# Revit family: ROTHOB_Rothoblaas_Screw_HBSPlate-HBSPL
name_source: partatom
category: Structural Connections
units: mm (PartAtom-declared; Revit-internal decimal feet)

## family parameters
Cut with Voids When Loaded = No
Enable cutting in views = Yes
Host = Face
Material for Model Behavior = Steel
OmniClass Number = 23.20.40.11.14.24
OmniClass Title = Screws
Shared = No

## types (18) — shared parameters
AssetType = Fixed
BIMObjectName = ROTHOB_Rothoblaas_Screw_HBSPlate-HBSPL
CECode = ETA-11/0030
CETitle = Rotho Blaas Self-tapping screws and threaded rods
Category = Pr_20_29_76_75: Self-tapping screws
CodePerformance = CE - Construction products
Color = Silver
Default Elevation = 1219.2 mm
Description = Pan head screws for plates
DurationUnit = Years
Esporta tipo in formato IFC con nome = IfcMechanicalFastenerType
ExpectedLife = 50
Features = Self-tapping screws for steel-timber connections
Finish = Zinc plated
HeadType = Reinforced pan head
ICC-ESCode = ESR-4645 | ELC-4645
ICC-ESTitle = Rotho blaas self-tapping wood screws | Rotho Blaas Self-tapping Wood Screws
IfcExportAs = IfcMechanicalFastenerType
IfcExportType = USERDEFINED
ManufacturerName = ROTHO BLAAS SRL
ManufacturerURL = www.rothoblaas.com
Material = Electrogalvanized carbon steel
ModelDisclaimer = The latest version of the data sheets can be found on our website
Name = Screw
ObjectMaterial = ROTHOB_Rothoblaas_CarbonSteel_Electrogalvanized
OmniClassCode = 23.20.40.11.14.24
OmniClassTitle = Screws
OmniClassVersion = 2012-05-16
ProductInformation = www.rothoblaas.com/products/fastening/screws/screws-carpentry/hbs-plate
Revision = 000
Shape = Cylindrical
Tipo IFC predefinito = USERDEFINED
UniClass2015Code = Pr_20_29_76_75
UniClass2015Title = Self-tapping screws
UniClass2015Version = Products v1.38
Version = 003

## per-type parameters (varying)
| type | BitType | GTIN | H1 | H2 | HeadDiameter_dk | HeadThickness_t1 | InsertionLength_L | MinWeight | ModelNumber | ModelNumberCode | NominalDiameter | NominalDiameter_d1 | NominalLength | ShankDiameter_ds | ShankLength | Size | ThreadDiameter_d2 | ThreadLength_b | ThreadRadius | TipLength | UnderheadDiameter | UnderheadLength | WasherThickness_tk |
| HBSPL860_8x60mm | 40 | 8059386079140 | 5 mm  [stored 0.0164042 ft] | 2.0141 mm  [stored 0.00660794 ft] | 13.5 mm  [stored 0.0442913 ft] | 13.5 mm  [stored 0.0442913 ft] | 60 mm | 0.014 kg | HBSPL860 | 860 | 8 mm  [stored 0.0262467 ft] | 8 mm  [stored 0.0262467 ft] | 60 mm | 6.3 mm  [stored 0.0206693 ft] | 1 mm  [stored 0.00328084 ft] | 8x60 mm | 5.9 mm  [stored 0.019357 ft] | 52 mm | 2.95 mm  [stored 0.00967848 ft] | 11.8318 mm  [stored 0.0388182 ft] | 10 mm  [stored 0.0328084 ft] | 4 mm  [stored 0.0131234 ft] | 4.5 mm  [stored 0.0147638 ft] |
| HBSPL880_8x80mm | 40 | 8059386079188 | 5 mm  [stored 0.0164042 ft] | 2.0141 mm  [stored 0.00660794 ft] | 13.5 mm  [stored 0.0442913 ft] | 13.5 mm  [stored 0.0442913 ft] | 80 mm | 0.027 kg | HBSPL880 | 880 | 8 mm  [stored 0.0262467 ft] | 8 mm  [stored 0.0262467 ft] | 80 mm | 6.3 mm  [stored 0.0206693 ft] | 14.9929 mm  [stored 0.0491893 ft] | 8x80 mm | 5.9 mm  [stored 0.019357 ft] | 55 mm  [stored 0.180446 ft] | 2.95 mm  [stored 0.00967848 ft] | 11.8318 mm  [stored 0.0388182 ft] | 10 mm  [stored 0.0328084 ft] | 4 mm  [stored 0.0131234 ft] | 4.5 mm  [stored 0.0147638 ft] |
| HBSPL8100_8x100mm | 40 | 8059386079164 | 5 mm  [stored 0.0164042 ft] | 2.0141 mm  [stored 0.00660794 ft] | 13.5 mm  [stored 0.0442913 ft] | 13.5 mm  [stored 0.0442913 ft] | 100 mm | 0.030 kg | HBSPL8100 | 8100 | 8 mm  [stored 0.0262467 ft] | 8 mm  [stored 0.0262467 ft] | 100 mm | 6.3 mm  [stored 0.0206693 ft] | 14.9929 mm  [stored 0.0491893 ft] | 8x100 mm | 5.9 mm  [stored 0.019357 ft] | 75 mm | 2.95 mm  [stored 0.00967848 ft] | 11.8318 mm  [stored 0.0388182 ft] | 10 mm  [stored 0.0328084 ft] | 4 mm  [stored 0.0131234 ft] | 4.5 mm  [stored 0.0147638 ft] |
| HBSPL8120_8x120mm | 40 | 8059386079058 | 5 mm  [stored 0.0164042 ft] | 2.0141 mm  [stored 0.00660794 ft] | 13.5 mm  [stored 0.0442913 ft] | 13.5 mm  [stored 0.0442913 ft] | 120 mm | 0.036 kg | HBSPL8120 | 8120 | 8 mm  [stored 0.0262467 ft] | 8 mm  [stored 0.0262467 ft] | 120 mm | 6.3 mm  [stored 0.0206693 ft] | 14.9929 mm  [stored 0.0491893 ft] | 8x120 mm | 5.9 mm  [stored 0.019357 ft] | 95 mm | 2.95 mm  [stored 0.00967848 ft] | 11.8318 mm  [stored 0.0388182 ft] | 10 mm  [stored 0.0328084 ft] | 4 mm  [stored 0.0131234 ft] | 4.5 mm  [stored 0.0147638 ft] |
| HBSPL8140_8x140mm | 40 | 8059386079195 | 5 mm  [stored 0.0164042 ft] | 2.0141 mm  [stored 0.00660794 ft] | 13.5 mm  [stored 0.0442913 ft] | 13.5 mm  [stored 0.0442913 ft] | 140 mm | 0.030 kg | HBSPL8140 | 8140 | 8 mm  [stored 0.0262467 ft] | 8 mm  [stored 0.0262467 ft] | 140 mm | 6.3 mm  [stored 0.0206693 ft] | 19.9929 mm  [stored 0.0655935 ft] | 8x140 mm | 5.9 mm  [stored 0.019357 ft] | 110 mm | 2.95 mm  [stored 0.00967848 ft] | 11.8318 mm  [stored 0.0388182 ft] | 10 mm  [stored 0.0328084 ft] | 4 mm  [stored 0.0131234 ft] | 4.5 mm  [stored 0.0147638 ft] |
| HBSPL8160_8x160mm | 40 | 8059386079089 | 5 mm  [stored 0.0164042 ft] | 2.0141 mm  [stored 0.00660794 ft] | 13.5 mm  [stored 0.0442913 ft] | 13.5 mm  [stored 0.0442913 ft] | 160 mm | 0.035 kg | HBSPL8160 | 8160 | 8 mm  [stored 0.0262467 ft] | 8 mm  [stored 0.0262467 ft] | 160 mm | 6.3 mm  [stored 0.0206693 ft] | 19.9929 mm  [stored 0.0655935 ft] | 8x160 mm | 5.9 mm  [stored 0.019357 ft] | 130 mm | 2.95 mm  [stored 0.00967848 ft] | 11.8318 mm  [stored 0.0388182 ft] | 10 mm  [stored 0.0328084 ft] | 4 mm  [stored 0.0131234 ft] | 4.5 mm  [stored 0.0147638 ft] |
| HBSPL1080_10x80mm | 40 | 8059386079201 | 6.5 mm | 1.5329 mm | 16.5 mm  [stored 0.0541339 ft] | 16.5 mm  [stored 0.0541339 ft] | 80 mm | 0.034 kg | HBSPL1080 | 1080 | 10 mm  [stored 0.0328084 ft] | 10 mm  [stored 0.0328084 ft] | 80 mm | 7.2 mm  [stored 0.023622 ft] | 7.7353 mm  [stored 0.0253783 ft] | 10x80 mm | 6.6 mm  [stored 0.0216535 ft] | 60 mm | 3.3 mm  [stored 0.0108268 ft] | 13.2356 mm  [stored 0.0434239 ft] | 12 mm  [stored 0.0393701 ft] | 5 mm  [stored 0.0164042 ft] | 5 mm  [stored 0.0164042 ft] |
| HBSPL10100_10x100mm | 40 | 8059386079072 | 6.5 mm | 1.5329 mm | 16.5 mm  [stored 0.0541339 ft] | 16.5 mm  [stored 0.0541339 ft] | 100 mm | 0.038 kg | HBSPL10100 | 10100 | 10 mm  [stored 0.0328084 ft] | 10 mm  [stored 0.0328084 ft] | 100 mm | 7.2 mm  [stored 0.023622 ft] | 12.7352 mm  [stored 0.0417822 ft] | 10x100 mm | 6.6 mm  [stored 0.0216535 ft] | 75 mm | 3.3 mm  [stored 0.0108268 ft] | 13.2356 mm  [stored 0.0434239 ft] | 12 mm  [stored 0.0393701 ft] | 5 mm  [stored 0.0164042 ft] | 5 mm  [stored 0.0164042 ft] |
| HBSPL10120_10x120mm | 40 | 8059386079133 | 6.5 mm | 1.5329 mm | 16.5 mm  [stored 0.0541339 ft] | 16.5 mm  [stored 0.0541339 ft] | 120 mm | 0.046 kg | HBSPL10120 | 10120 | 10 mm  [stored 0.0328084 ft] | 10 mm  [stored 0.0328084 ft] | 120 mm | 7.2 mm  [stored 0.023622 ft] | 12.7352 mm  [stored 0.0417822 ft] | 10x120 mm | 6.6 mm  [stored 0.0216535 ft] | 95 mm | 3.3 mm  [stored 0.0108268 ft] | 13.2356 mm  [stored 0.0434239 ft] | 12 mm  [stored 0.0393701 ft] | 5 mm  [stored 0.0164042 ft] | 5 mm  [stored 0.0164042 ft] |
| HBSPL10140_10x140mm | 40 | 8059386079065 | 6.5 mm | 1.5329 mm | 16.5 mm  [stored 0.0541339 ft] | 16.5 mm  [stored 0.0541339 ft] | 140 mm | 0.047 kg | HBSPL10140 | 10140 | 10 mm  [stored 0.0328084 ft] | 10 mm  [stored 0.0328084 ft] | 140 mm | 7.2 mm  [stored 0.023622 ft] | 17.7353 mm | 10x140 mm | 6.6 mm  [stored 0.0216535 ft] | 110 mm | 3.3 mm  [stored 0.0108268 ft] | 13.2356 mm  [stored 0.0434239 ft] | 12 mm  [stored 0.0393701 ft] | 5 mm  [stored 0.0164042 ft] | 5 mm  [stored 0.0164042 ft] |
| HBSPL10160_10x160mm | 40 | 8059386079102 | 6.5 mm | 1.5329 mm | 16.5 mm  [stored 0.0541339 ft] | 16.5 mm  [stored 0.0541339 ft] | 160 mm | 0.058 kg | HBSPL10160 | 10160 | 10 mm  [stored 0.0328084 ft] | 10 mm  [stored 0.0328084 ft] | 160 mm | 7.2 mm  [stored 0.023622 ft] | 17.7353 mm | 10x160 mm | 6.6 mm  [stored 0.0216535 ft] | 130 mm | 3.3 mm  [stored 0.0108268 ft] | 13.2356 mm  [stored 0.0434239 ft] | 12 mm  [stored 0.0393701 ft] | 5 mm  [stored 0.0164042 ft] | 5 mm  [stored 0.0164042 ft] |
| HBSPL10180_10x180mm | 40 | 8059386079157 | 6.5 mm | 1.5329 mm | 16.5 mm  [stored 0.0541339 ft] | 16.5 mm  [stored 0.0541339 ft] | 180 mm | 0.060 kg | HBSPL10180 | 10180 | 10 mm  [stored 0.0328084 ft] | 10 mm  [stored 0.0328084 ft] | 180 mm | 7.2 mm  [stored 0.023622 ft] | 17.7353 mm | 10x180 mm | 6.6 mm  [stored 0.0216535 ft] | 150 mm | 3.3 mm  [stored 0.0108268 ft] | 13.2356 mm  [stored 0.0434239 ft] | 12 mm  [stored 0.0393701 ft] | 5 mm  [stored 0.0164042 ft] | 5 mm  [stored 0.0164042 ft] |
| HBSPL12100_12x100mm | 50 | 8059386079171 | 8 mm  [stored 0.0262467 ft] | 2.4209 mm  [stored 0.00794259 ft] | 18.5 mm  [stored 0.0606955 ft] | 19.5 mm  [stored 0.0639764 ft] | 100 mm | 0.050 kg | HBSPL12100 | 12100 | 12 mm  [stored 0.0393701 ft] | 12 mm  [stored 0.0393701 ft] | 100 mm | 8.55 mm  [stored 0.0280512 ft] | 9.7949 mm  [stored 0.0321355 ft] | 12x100 mm | 7.3 mm  [stored 0.0239501 ft] | 75 mm | 3.65 mm  [stored 0.0119751 ft] | 14.6393 mm | 13 mm | 6 mm  [stored 0.019685 ft] | 5.5 mm  [stored 0.0180446 ft] |
| HBSPL12120_12x120mm | 50 | 8059386079232 | 8 mm  [stored 0.0262467 ft] | 2.4209 mm  [stored 0.00794259 ft] | 18.5 mm  [stored 0.0606955 ft] | 19.5 mm  [stored 0.0639764 ft] | 120 mm | 0.063 kg | HBSPL12120 | 12120 | 12 mm  [stored 0.0393701 ft] | 12 mm  [stored 0.0393701 ft] | 120 mm | 8.55 mm  [stored 0.0280512 ft] | 14.7888 mm  [stored 0.0485197 ft] | 12x120 mm | 7.3 mm  [stored 0.0239501 ft] | 90 mm | 3.65 mm  [stored 0.0119751 ft] | 14.6393 mm | 13 mm | 6 mm  [stored 0.019685 ft] | 5.5 mm  [stored 0.0180446 ft] |
| HBSPL12140_12x140mm | 50 | 8059386079126 | 8 mm  [stored 0.0262467 ft] | 2.4209 mm  [stored 0.00794259 ft] | 18.5 mm  [stored 0.0606955 ft] | 19.5 mm  [stored 0.0639764 ft] | 140 mm | 0.070 kg | HBSPL12140 | 12140 | 12 mm  [stored 0.0393701 ft] | 12 mm  [stored 0.0393701 ft] | 140 mm | 8.55 mm  [stored 0.0280512 ft] | 14.7888 mm  [stored 0.0485197 ft] | 12x140 mm | 7.3 mm  [stored 0.0239501 ft] | 110 mm | 3.65 mm  [stored 0.0119751 ft] | 14.6393 mm | 13 mm | 6 mm  [stored 0.019685 ft] | 5.5 mm  [stored 0.0180446 ft] |
| HBSPL12160_12x160mm | 50 | 8059386079096 | 8 mm  [stored 0.0262467 ft] | 2.4209 mm  [stored 0.00794259 ft] | 18.5 mm  [stored 0.0606955 ft] | 19.5 mm  [stored 0.0639764 ft] | 160 mm | 0.078 kg | HBSPL12160 | 12160 | 12 mm  [stored 0.0393701 ft] | 12 mm  [stored 0.0393701 ft] | 160 mm | 8.55 mm  [stored 0.0280512 ft] | 24.7888 mm  [stored 0.0813281 ft] | 12x160 mm | 7.3 mm  [stored 0.0239501 ft] | 120 mm | 3.65 mm  [stored 0.0119751 ft] | 14.6393 mm | 13 mm | 6 mm  [stored 0.019685 ft] | 5.5 mm  [stored 0.0180446 ft] |
| HBSPL12180_12x180mm | 50 | 8059386079041 | 8 mm  [stored 0.0262467 ft] | 2.4209 mm  [stored 0.00794259 ft] | 18.5 mm  [stored 0.0606955 ft] | 19.5 mm  [stored 0.0639764 ft] | 180 mm | 0.086 kg | HBSPL12180 | 12180 | 12 mm  [stored 0.0393701 ft] | 12 mm  [stored 0.0393701 ft] | 180 mm | 8.55 mm  [stored 0.0280512 ft] | 24.7888 mm  [stored 0.0813281 ft] | 12x180 mm | 7.3 mm  [stored 0.0239501 ft] | 140 mm | 3.65 mm  [stored 0.0119751 ft] | 14.6393 mm | 13 mm | 6 mm  [stored 0.019685 ft] | 5.5 mm  [stored 0.0180446 ft] |
| HBSPL12200_12x200mm | 50 | 8059386079119 | 8 mm  [stored 0.0262467 ft] | 2.4209 mm  [stored 0.00794259 ft] | 18.5 mm  [stored 0.0606955 ft] | 19.5 mm  [stored 0.0639764 ft] | 200 mm | 0.094 kg | HBSPL12200 | 12200 | 12 mm  [stored 0.0393701 ft] | 12 mm  [stored 0.0393701 ft] | 200 mm | 8.55 mm  [stored 0.0280512 ft] | 24.7888 mm  [stored 0.0813281 ft] | 12x200 mm | 7.3 mm  [stored 0.0239501 ft] | 160 mm | 3.65 mm  [stored 0.0119751 ft] | 14.6393 mm | 13 mm | 6 mm  [stored 0.019685 ft] | 5.5 mm  [stored 0.0180446 ft] |

note: [stored X ft] marks values corroborated as IEEE doubles in the binary element streams (Revit-internal decimal feet)
